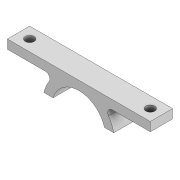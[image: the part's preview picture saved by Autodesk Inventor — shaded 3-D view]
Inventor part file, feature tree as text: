
AUTODESK INVENTOR PART (.ipt)
format: ipt  version: 2022 (Build 260153000, 153)  size: 121,856 bytes
history: native  units: mm
features: extrude x2, sketch x1
ambient origin geometry x8: Origin, YZ Plane, XZ Plane, XY Plane, X Axis, Y Axis, Z Axis, Center Point
bodies: Solid1 (feature_tree)
feature tree (3):
  extrude  "Extrusion1"  Depth=5.0mm
  extrude  "Extrusion3"  Depth=2.0mm
  sketch  "Sketch3"  dims[d5=5.0mm d6=0.0mm d12=12.0mm d13=2.0mm d14=16.0mm d15=16.0mm d16=6.0mm d17=4.0mm d18=6.0mm d19=4.0mm d20=1.0mm d21=1.0mm d31=2.0mm d32=2.5mm d33=2.5mm d34=2.0mm d35=2.5mm d36=2.5mm d37=5.0mm d38=0.0mm d39=13.0mm d40=13.0mm]
